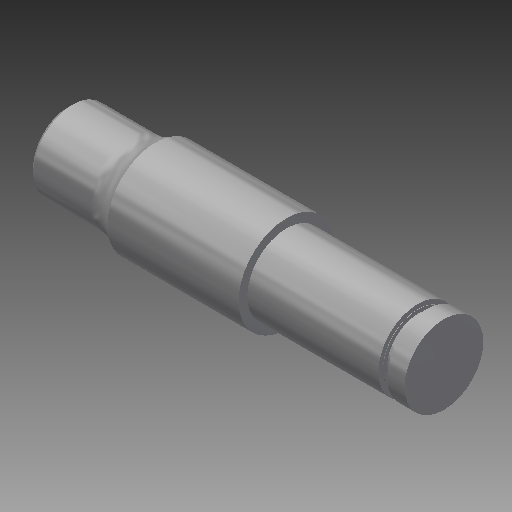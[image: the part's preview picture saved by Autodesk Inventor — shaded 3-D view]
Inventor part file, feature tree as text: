
AUTODESK INVENTOR PART (.ipt)
format: ipt  version: 2019 (Build 230136000, 136)  size: 160,768 bytes
history: native  units: mm
features: other x6, chamfer x1, fillet x1
ambient origin geometry x6: Origin, XZ Plane, XY Plane, X Axis, Y Axis, Z Axis
bodies: Body1 (feature_tree)
feature tree (8):
  other  "實體1"
  other  "迴轉1"
  chamfer  "倒角1"  [1 undecoded]
  fillet  "圓角1"  Radius=9.0mm
  other  "扣環槽1"
  other  "起始平面"
  other  "主要草圖"
  other  "iFeature27:1"
note: 1 required parameter value undecoded (feature->parameter linkage not recoverable at this tier; creation-order binding heuristic only, values carry confidence <= 0.55)
